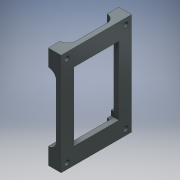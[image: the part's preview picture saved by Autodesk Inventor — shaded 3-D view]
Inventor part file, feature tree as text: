
AUTODESK INVENTOR PART (.ipt)
format: ipt  version: 2016 (Build 200138000, 138)  size: 235,008 bytes
history: native  units: mm
features: extrude x6, sketch x6, fillet x4, projected_geometry x3
ambient origin geometry x8: Origin, YZ Plane, XZ Plane, XY Plane, X Axis, Y Axis, Z Axis, Center Point
bodies: Solid1 (feature_tree)
feature tree (19):
  extrude  "Extrusion1"  Depth=13.0mm
  extrude  "Extrusion3"  Depth=8.0mm
  extrude  "Extrusion5"  Depth=8.0mm
  extrude  "Extrusion6"  Depth=8.0mm
  extrude  "Extrusion7"  Depth=8.0mm TaperAngle=0.0deg
  fillet  "Fillet1"  Radius=5.0mm
  fillet  "Fillet2"  Radius=6.0mm
  fillet  "Fillet3"  Radius=6.0mm
  extrude  "Extrusion8"  Depth=5.0mm
  fillet  "Fillet4"  Radius=5.0mm
  sketch  "Sketch1"  dims[d0=104.0mm d1=13.0mm]
  sketch  "Sketch3"  dims[d2=12.0mm d3=8.0mm]
  projected_geometry  "Projected Loop1"
  sketch  "Sketch4"  dims[d4=80.0mm d5=8.0mm]
  projected_geometry  "Projected Loop2"
  sketch  "Sketch5"  dims[d6=72.0mm d7=0.0mm d14=8.0mm]
  projected_geometry  "Projected Loop3"
  sketch  "Sketch6"  dims[d15=8.0mm d16=8.0mm d17=0.0mm d18=5.0mm d19=6.0mm d20=6.0mm]
  sketch  "Sketch7"  dims[d25=5.0mm d31=5.0mm d32=5.0mm d37=6.0mm d38=6.0mm d46=6.0mm d47=6.0mm d48=10.0mm d49=0.0mm d50=5.0mm d51=5.0mm d52=5.0mm d53=5.0mm d54=10.0mm d55=0.0mm d56=12.0mm d57=12.0mm d58=8.0mm d59=0.0mm d60=8.0mm d61=8.0mm d62=8.0mm d63=17.0mm d64=17.0mm d65=72.0mm d66=8.0mm d67=0.0mm d68=8.0mm]
